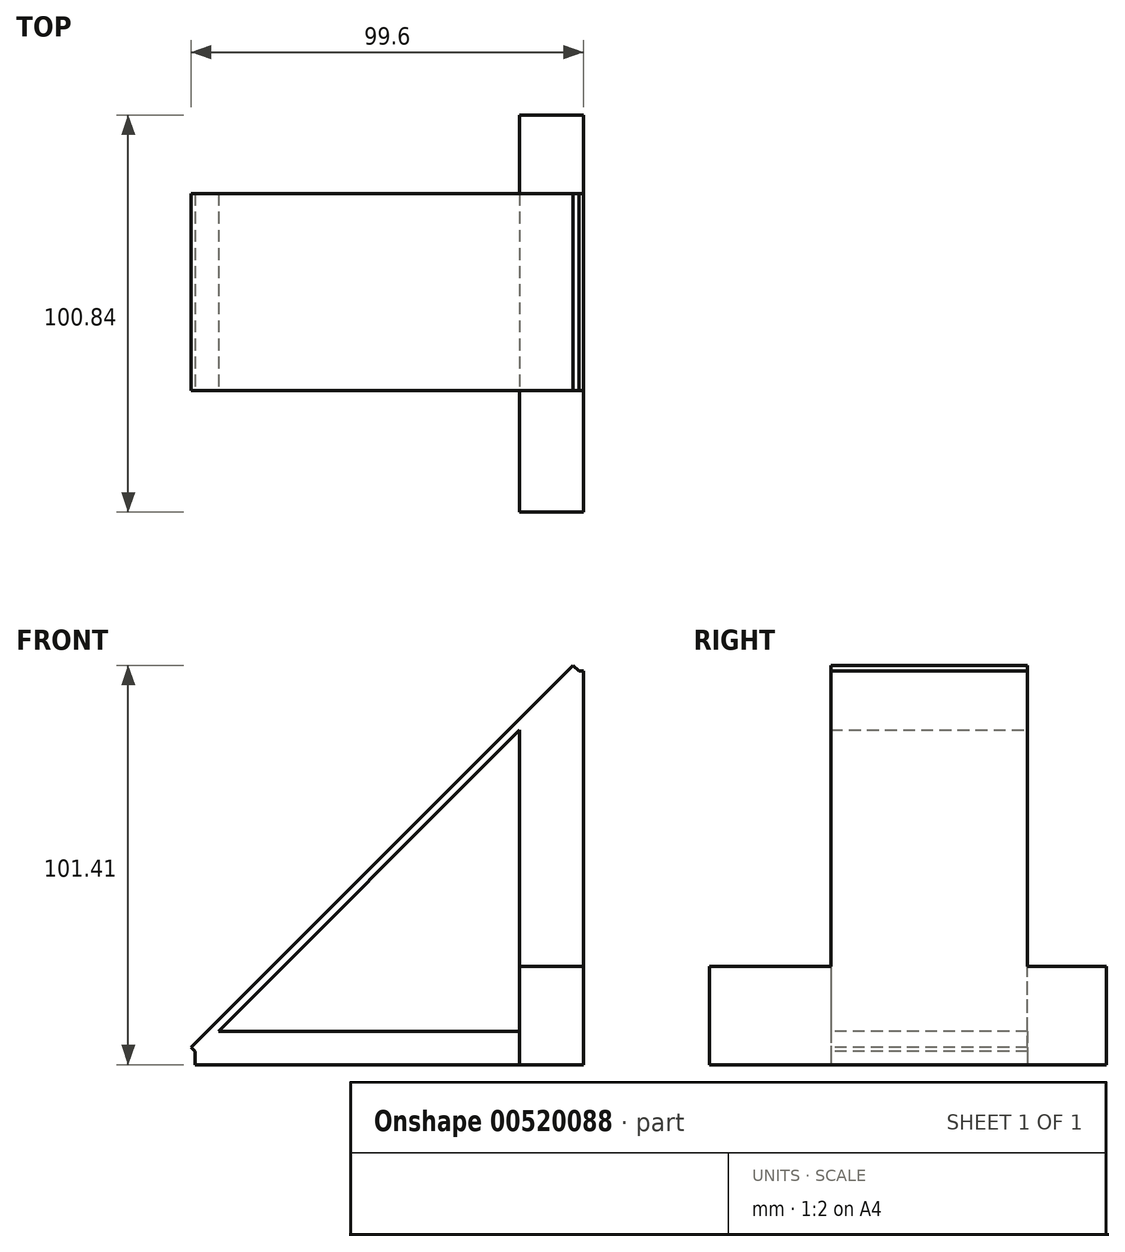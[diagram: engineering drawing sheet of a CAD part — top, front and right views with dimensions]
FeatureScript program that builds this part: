
annotation { "Feature Type Name" : "Feature", "Feature Type Description" : "" }
export const myFeature = defineFeature(function(context is Context, id is Id, definition is map)
    precondition{}
    {
        {
            var Q0;
            Q0=qCreatedBy(makeId("Top.planeOp"),FACE);
            var sketch = newSketch(context, id + "F0", { "sketchPlane" : qUnion([Q0])});
            skLineSegment(sketch, "E0.bottom", {"start": v(-23.8, 33.85) * mm, "end": v(76.2, 33.85) * mm});
            skLineSegment(sketch, "E0.top", {"start": v(-23.8, -16.15) * mm, "end": v(76.2, -16.15) * mm});
            skLineSegment(sketch, "E0.left", {"start": v(-23.8, 33.85) * mm, "end": v(-23.8, -16.15) * mm});
            skLineSegment(sketch, "E0.right", {"start": v(76.2, 33.85) * mm, "end": v(76.2, -16.15) * mm});
            skLineSegment(sketch, "E1.bottom", {"start": v(58.67, 53.82) * mm, "end": v(74.82, 53.82) * mm});
            skLineSegment(sketch, "E1.top", {"start": v(58.67, -47.02) * mm, "end": v(74.82, -47.02) * mm});
            skLineSegment(sketch, "E1.left", {"start": v(58.67, 53.82) * mm, "end": v(58.67, -47.02) * mm});
            skLineSegment(sketch, "E1.right", {"start": v(74.82, 53.82) * mm, "end": v(74.82, -47.02) * mm});
            skSolve(sketch);
        }
        {
            var Q0;
            {var subQ0=sQuery(id+"F0.wireOp",EDGE,"E1.left");var subQ1=sQuery(id+"F0.wireOp",EDGE,"E0.bottom");var subQ2=makeQuery(id+"F0.imprint","INTERSECT",VERTEX,{"derivedFrom":[subQ1,subQ0]});Q0=makeQuery(id+"F0.imprint","IMPRINT",FACE,{"disambiguationData":[TD([[makeQuery(id+"F0.imprint","IMPRINT",EDGE,{"disambiguationData":[TD([[subQ2,-1.0]])],"derivedFrom":subQ1}),-1.0]])]});}
            extrude(context, id + "F1", {"entities" : qUnion([Q0]), "depth" : 100 * mm, "offsetDistance" : 25 * mm});
        }
        {
            var Q0;
            {var subQ0=sQuery(id+"F0.wireOp",EDGE,"E0.left");Q0=makeQuery(id+"F0.imprint","IMPRINT",FACE,{"disambiguationData":[TD([[makeQuery(id+"F0.imprint","IMPRINT",EDGE,{"derivedFrom":subQ0}),1.0]])]});}
            extrude(context, id + "F2", {"entities" : qUnion([Q0]), "operationType" : NewBodyOperationType.ADD, "depth" : 8.5 * mm, "offsetDistance" : 25 * mm});
        }
        {
            var Q0;
            Q0=makeQuery(id+"F1.opExtrude","CAP_EDGE",EDGE,{"disambiguationData":[OSD([sQuery(id+"F0.wireOp",EDGE,"E1.left")])],"isStart":false});
            chamfer(context, id + "F3", {"entities" : qUnion([Q0]), "width" : 15 * mm, "tangentPropagation" : true});
        }
        {
            var Q0;
            Q0=makeQuery(id+"F3.opChamfer","BLEND_FACE",FACE,{"disambiguationData":[OSD([sQuery(id+"F0.wireOp",EDGE,"E1.left")])]});
            var sketch = newSketch(context, id + "F4", { "sketchPlane" : qUnion([Q0])});
            skLineSegment(sketch, "E2.bottom", {"start": v(-33.85, 122.8) * mm, "end": v(16.15, 122.8) * mm});
            skLineSegment(sketch, "E2.top", {"start": v(-33.85, -14.42) * mm, "end": v(16.15, -14.42) * mm});
            skLineSegment(sketch, "E2.left", {"start": v(-33.85, 122.8) * mm, "end": v(-33.85, -14.42) * mm});
            skLineSegment(sketch, "E2.right", {"start": v(16.15, 122.8) * mm, "end": v(16.15, -14.42) * mm});
            skSolve(sketch);
        }
        {
            var Q0;
            Q0 = qSketchRegion(id + "F4", true);
            extrude(context, id + "F5", {"entities" : qUnion([Q0]), "operationType" : NewBodyOperationType.REMOVE, "depth" : 28 * mm, "offsetDistance" : 25 * mm});
        }
        {
            var Q0;
            {var subQ0=sQuery(id+"F4.wireOp",EDGE,"E2.bottom");Q0=makeQuery(id+"F4.imprint","IMPRINT",FACE,{"disambiguationData":[TD([[makeQuery(id+"F4.imprint","IMPRINT",EDGE,{"derivedFrom":subQ0}),-1.0]])]});}
            var Q1;
            {var subQ0=sQuery(id+"F4.wireOp",EDGE,"E2.top");Q1=makeQuery(id+"F4.imprint","IMPRINT",FACE,{"disambiguationData":[TD([[makeQuery(id+"F4.imprint","IMPRINT",EDGE,{"derivedFrom":subQ0}),1.0]])]});}
            extrude(context, id + "F6", {"entities" : qUnion([Q0, Q1]), "operationType" : NewBodyOperationType.ADD, "depth" : 2 * mm, "offsetDistance" : 25 * mm});
        }
        {
            var Q0;
            {var subQ5=sQuery(id+"F0.wireOp",EDGE,"E1.top");Q0=makeQuery(id+"F0.imprint","IMPRINT",FACE,{"disambiguationData":[TD([[makeQuery(id+"F0.imprint","IMPRINT",EDGE,{"derivedFrom":subQ5}),1.0]])]});}
            var Q1;
            {var subQ5=sQuery(id+"F0.wireOp",EDGE,"E1.bottom");Q1=makeQuery(id+"F0.imprint","IMPRINT",FACE,{"disambiguationData":[TD([[makeQuery(id+"F0.imprint","IMPRINT",EDGE,{"derivedFrom":subQ5}),-1.0]])]});}
            extrude(context, id + "F7", {"entities" : qUnion([Q0, Q1]), "operationType" : NewBodyOperationType.ADD, "depth" : 25 * mm, "offsetDistance" : 25 * mm});
        }
    });
